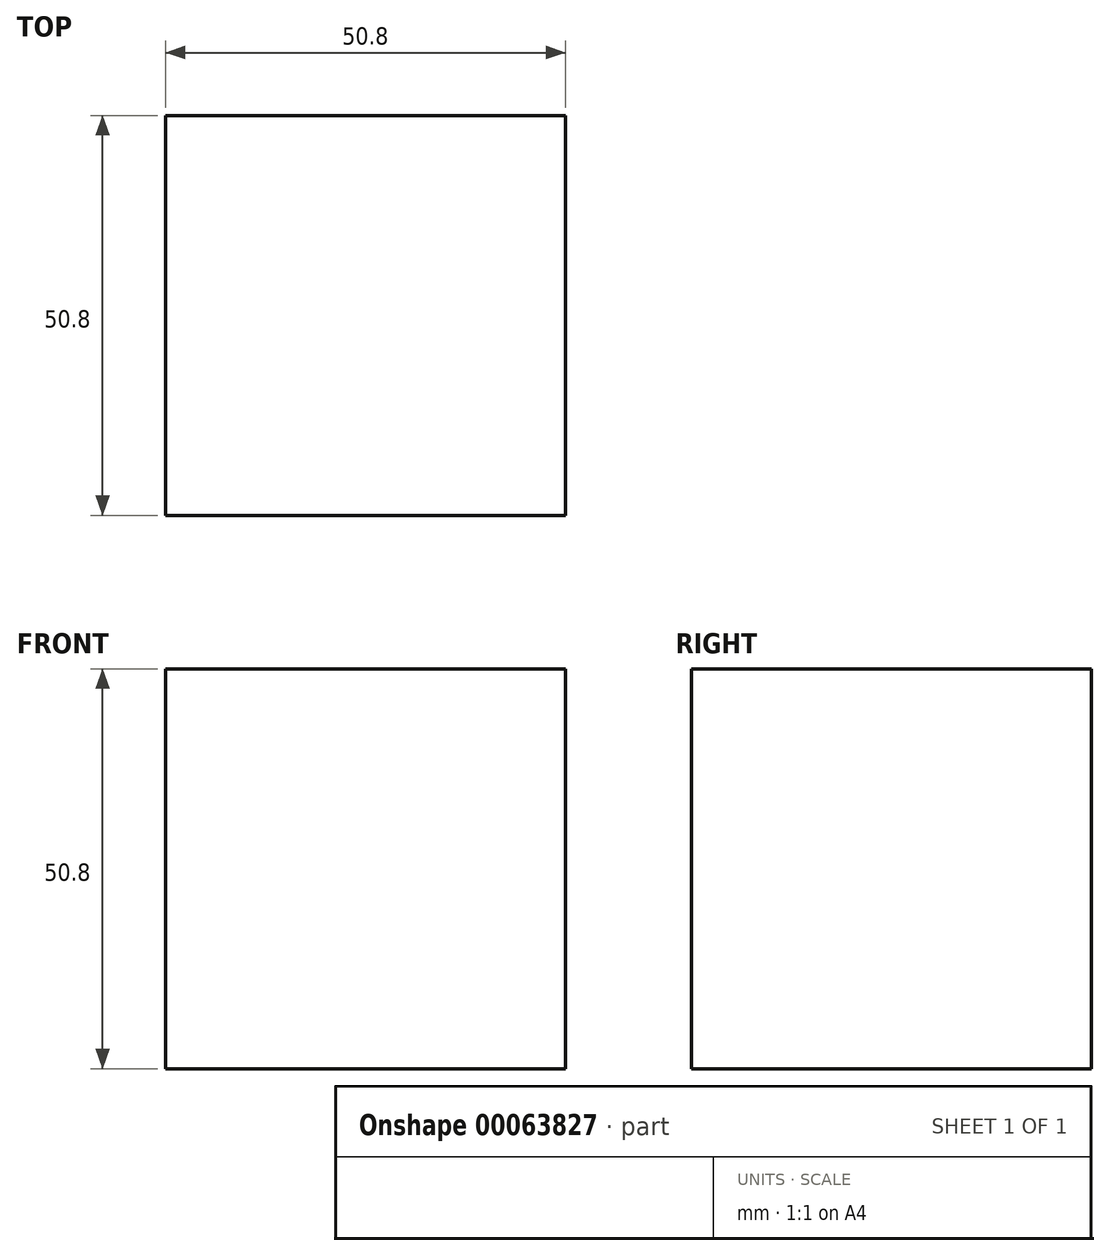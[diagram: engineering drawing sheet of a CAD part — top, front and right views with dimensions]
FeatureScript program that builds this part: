
annotation { "Feature Type Name" : "Feature", "Feature Type Description" : "" }
export const myFeature = defineFeature(function(context is Context, id is Id, definition is map)
    precondition{}
    {
        {
            var Q0;
            Q0=qCreatedBy(makeId("Front.planeOp"),FACE);
            var sketch = newSketch(context, id + "F0", { "sketchPlane" : qUnion([Q0])});
            skLineSegment(sketch, "E0.bottom", {"start": v(-3.48, 2.69) * mm, "end": v(47.32, 2.69) * mm});
            skLineSegment(sketch, "E0.top", {"start": v(-3.48, 53.49) * mm, "end": v(47.32, 53.49) * mm});
            skLineSegment(sketch, "E0.left", {"start": v(-3.48, 2.69) * mm, "end": v(-3.48, 53.49) * mm});
            skLineSegment(sketch, "E0.right", {"start": v(47.32, 2.69) * mm, "end": v(47.32, 53.49) * mm});
            skSolve(sketch);
        }
        {
            var Q0;
            Q0=makeQuery(id+"F0.imprint","IMPRINT",FACE,{"disambiguationData":[TD([[makeQuery(id+"F0.imprint","IMPRINT",EDGE,{"derivedFrom":sQuery(id+"F0.wireOp",EDGE,"E0.bottom")}),1.0]])]});
            extrude(context, id + "F1", {"entities" : qUnion([Q0]), "depth" : 50.8 * mm, "hasDraft" : true, "draftAngle" : 0 * degree});
        }
    });
